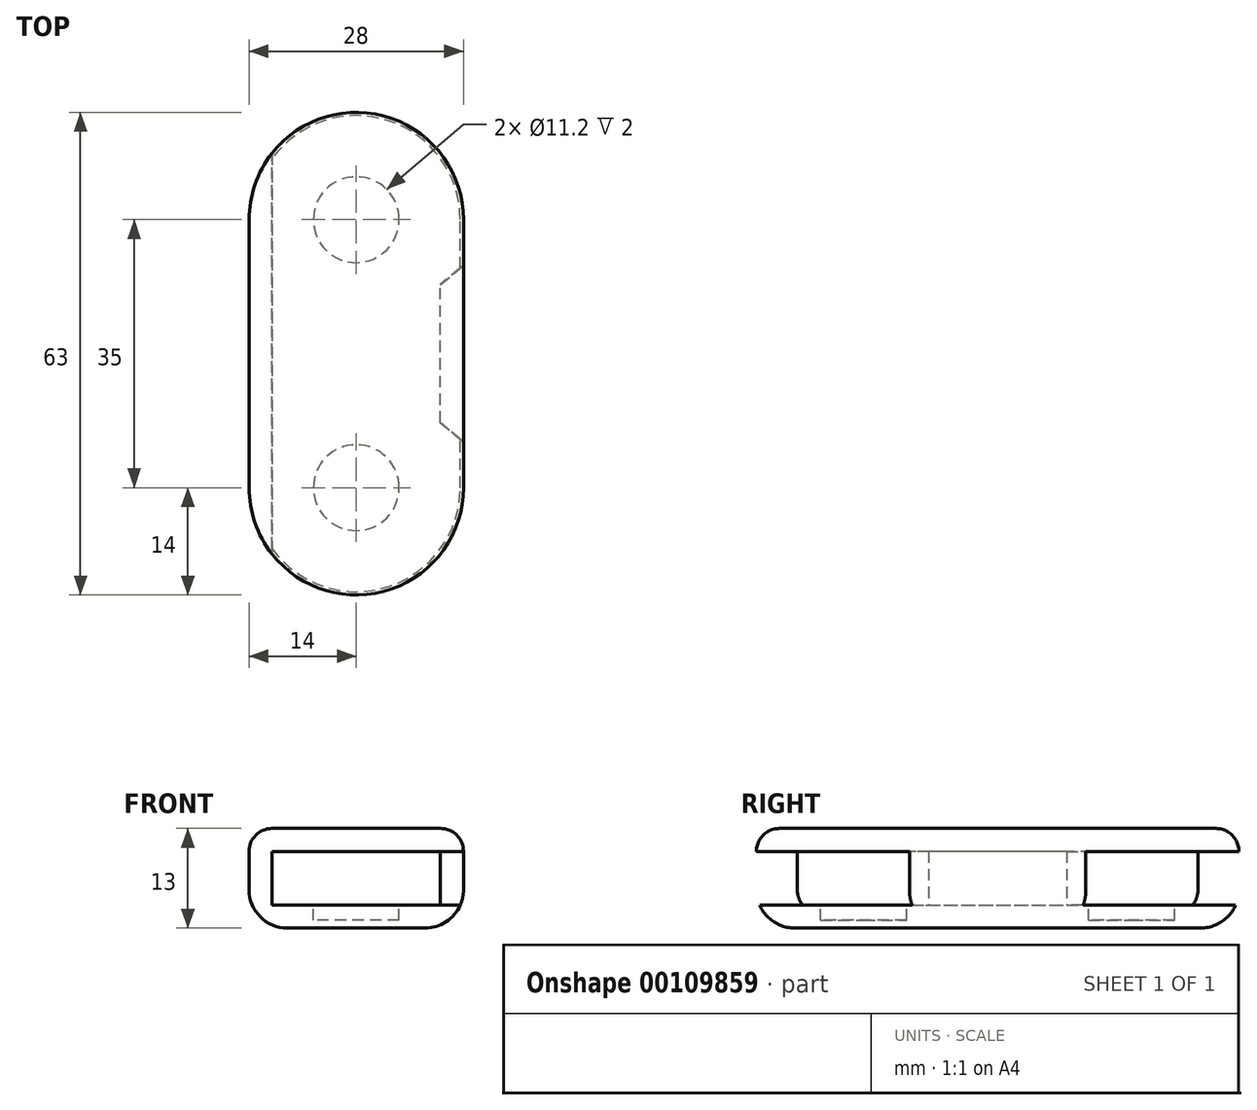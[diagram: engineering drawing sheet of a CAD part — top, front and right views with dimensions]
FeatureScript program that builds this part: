
annotation { "Feature Type Name" : "Feature", "Feature Type Description" : "" }
export const myFeature = defineFeature(function(context is Context, id is Id, definition is map)
    precondition{}
    {
        {
            var Q0;
            Q0=qCreatedBy(makeId("Top.planeOp"),FACE);
            var sketch = newSketch(context, id + "F0", { "sketchPlane" : qUnion([Q0])});
            skCircle(sketch, "E0", {"center": v(0, 17.5) * mm, "radius": 5.6 * mm, "construction": true});
            skCircle(sketch, "E1", {"center": v(0, -17.5) * mm, "radius": 5.6 * mm, "construction": true});
            skLineSegment(sketch, "E2", {"start": v(0, 17.5) * mm, "end": v(0, -17.5) * mm, "construction": true});
            skArc(sketch, "E3", {"start": v(11, 17.5) * mm, "mid": v(0, 28.5) * mm, "end": v(-11, 17.5) * mm, "construction": true});
            skArc(sketch, "E4", {"start": v(-11, -17.5) * mm, "mid": v(0, -28.5) * mm, "end": v(11, -17.5) * mm, "construction": true});
            skLineSegment(sketch, "E5", {"start": v(-11, 17.5) * mm, "end": v(-11, -17.5) * mm, "construction": true});
            skLineSegment(sketch, "E6", {"start": v(11, 17.5) * mm, "end": v(11, -17.5) * mm, "construction": true});
            skArc(sketch, "E7.0", {"start": v(14, 17.5) * mm, "mid": v(0, 31.5) * mm, "end": v(-14, 17.5) * mm});
            skLineSegment(sketch, "E7.1", {"start": v(14, 17.5) * mm, "end": v(14, -17.5) * mm});
            skArc(sketch, "E7.2", {"start": v(-14, -17.5) * mm, "mid": v(0, -31.5) * mm, "end": v(14, -17.5) * mm});
            skLineSegment(sketch, "E7.3", {"start": v(-14, 17.5) * mm, "end": v(-14, -17.5) * mm});
            skLineSegment(sketch, "E8", {"start": v(-9, 25.87) * mm, "end": v(7.6, 32.12) * mm, "construction": true});
            skLineSegment(sketch, "E9", {"start": v(-9, -25.87) * mm, "end": v(7.6, -32.12) * mm, "construction": true});
            skArc(sketch, "E10", {"start": v(-15.3, 18.34) * mm, "mid": v(-17, 0) * mm, "end": v(-15.3, -18.34) * mm, "construction": true});
            skArc(sketch, "E11", {"start": v(15.66, 25.73) * mm, "mid": v(14, 0) * mm, "end": v(15.66, -25.73) * mm, "construction": true});
            skArc(sketch, "E12", {"start": v(7.6, 32.12) * mm, "mid": v(13.44, 31.2) * mm, "end": v(15.66, 25.73) * mm, "construction": true});
            skArc(sketch, "E13", {"start": v(7.6, -32.12) * mm, "mid": v(13.44, -31.2) * mm, "end": v(15.66, -25.73) * mm, "construction": true});
            skLineSegment(sketch, "E14", {"start": v(0, 0) * mm, "end": v(83, 0) * mm, "construction": true});
            skLineSegment(sketch, "E15", {"start": v(9.71, 26.5) * mm, "end": v(9.71, -26.5) * mm, "construction": true});
            skPoint(sketch, "E16.visualSharp", {"position": v(-14.1, 23.95) * mm});
            skArc(sketch, "E16.filletArc", {"start": v(-9, 25.87) * mm, "mid": v(-13.14, 22.93) * mm, "end": v(-15.3, 18.34) * mm, "construction": true});
            skPoint(sketch, "E17.visualSharp", {"position": v(-14.1, -23.95) * mm});
            skArc(sketch, "E17.filletArc", {"start": v(-15.3, -18.34) * mm, "mid": v(-13.14, -22.93) * mm, "end": v(-9, -25.87) * mm, "construction": true});
            skSolve(sketch);
        }
        {
            var Q0;
            Q0=makeQuery(id+"F0.imprint","IMPRINT",FACE,{"disambiguationData":[TD([[makeQuery(id+"F0.imprint","IMPRINT",EDGE,{"derivedFrom":sQuery(id+"F0.wireOp",EDGE,"E7.0")}),1.0]])]});
            extrude(context, id + "F1", {"entities" : qUnion([Q0]), "depth" : 3 * mm});
        }
        {
            var Q0;
            Q0=makeQuery(id+"F1.opExtrude","CAP_FACE",FACE,{"disambiguationData":[OSD([sQuery(id+"F0.wireOp",EDGE,"E7.0"),sQuery(id+"F0.wireOp",EDGE,"E7.1"),sQuery(id+"F0.wireOp",EDGE,"E7.2"),sQuery(id+"F0.wireOp",EDGE,"E7.3")])],"isStart":false});
            var sketch = newSketch(context, id + "F2", { "sketchPlane" : qUnion([Q0])});
            skCircle(sketch, "E18", {"center": v(0, 17.5) * mm, "radius": 5.6 * mm});
            skCircle(sketch, "E19", {"center": v(0, -17.5) * mm, "radius": 5.6 * mm});
            skLineSegment(sketch, "E20", {"start": v(0, 17.5) * mm, "end": v(0, -17.5) * mm, "construction": true});
            skArc(sketch, "E21", {"start": v(11, 17.5) * mm, "mid": v(0, 28.5) * mm, "end": v(-11, 17.5) * mm, "construction": true});
            skArc(sketch, "E22", {"start": v(-11, -17.5) * mm, "mid": v(0, -28.5) * mm, "end": v(11, -17.5) * mm, "construction": true});
            skLineSegment(sketch, "E23", {"start": v(-11, 17.5) * mm, "end": v(-11, -17.5) * mm, "construction": true});
            skLineSegment(sketch, "E24", {"start": v(11, 17.5) * mm, "end": v(11, -17.5) * mm, "construction": true});
            skArc(sketch, "E25.0", {"start": v(14, 17.5) * mm, "mid": v(0, 31.5) * mm, "end": v(-14, 17.5) * mm});
            skLineSegment(sketch, "E25.1", {"start": v(14, 17.5) * mm, "end": v(14, -17.5) * mm});
            skArc(sketch, "E25.2", {"start": v(-14, -17.5) * mm, "mid": v(0, -31.5) * mm, "end": v(14, -17.5) * mm});
            skLineSegment(sketch, "E25.3", {"start": v(-14, 17.5) * mm, "end": v(-14, -17.5) * mm});
            skLineSegment(sketch, "E26", {"start": v(-7.8, 25.97) * mm, "end": v(13.49, 36.11) * mm, "construction": true});
            skLineSegment(sketch, "E27", {"start": v(-7.8, -25.97) * mm, "end": v(13.49, -36.11) * mm, "construction": true});
            skArc(sketch, "E28", {"start": v(-10.24, 23.4) * mm, "mid": v(-15, 0) * mm, "end": v(-10.24, -23.4) * mm, "construction": true});
            skArc(sketch, "E29", {"start": v(19, 31.25) * mm, "mid": v(14, 0) * mm, "end": v(19, -31.25) * mm, "construction": true});
            skArc(sketch, "E30", {"start": v(13.49, 36.11) * mm, "mid": v(17.85, 35.5) * mm, "end": v(19, 31.25) * mm, "construction": true});
            skArc(sketch, "E31", {"start": v(13.49, -36.11) * mm, "mid": v(17.85, -35.5) * mm, "end": v(19, -31.25) * mm, "construction": true});
            skLineSegment(sketch, "E32", {"start": v(0, 0) * mm, "end": v(45, 0) * mm, "construction": true});
            skLineSegment(sketch, "E33", {"start": v(15.2, 32.5) * mm, "end": v(15.2, -32.5) * mm, "construction": true});
            skPoint(sketch, "E34.visualSharp", {"position": v(-9.46, 25.18) * mm});
            skArc(sketch, "E34.filletArc", {"start": v(-7.8, 25.97) * mm, "mid": v(-9.25, 24.92) * mm, "end": v(-10.24, 23.4) * mm, "construction": true});
            skPoint(sketch, "E35.visualSharp", {"position": v(-9.46, -25.18) * mm});
            skArc(sketch, "E35.filletArc", {"start": v(-10.24, -23.4) * mm, "mid": v(-9.25, -24.92) * mm, "end": v(-7.8, -25.97) * mm, "construction": true});
            skSolve(sketch);
        }
        {
            var Q0;
            Q0=makeQuery(id+"F2.imprint","IMPRINT",FACE,{"disambiguationData":[TD([[makeQuery(id+"F2.imprint","IMPRINT",EDGE,{"derivedFrom":sQuery(id+"F2.wireOp",EDGE,"E18")}),1.0]])]});
            var Q1;
            Q1=makeQuery(id+"F2.imprint","IMPRINT",FACE,{"disambiguationData":[TD([[makeQuery(id+"F2.imprint","IMPRINT",EDGE,{"derivedFrom":sQuery(id+"F2.wireOp",EDGE,"E19")}),1.0]])]});
            extrude(context, id + "F3", {"entities" : qUnion([Q0, Q1]), "operationType" : NewBodyOperationType.REMOVE, "oppositeDirection" : true, "depth" : 2 * mm});
        }
        {
            var Q0;
            Q0=qCreatedBy(makeId("Top.planeOp"),FACE);
            var sketch = newSketch(context, id + "F4", { "sketchPlane" : qUnion([Q0])});
            skCircle(sketch, "E36", {"center": v(0, 17.5) * mm, "radius": 5.6 * mm, "construction": true});
            skCircle(sketch, "E37", {"center": v(0, -17.5) * mm, "radius": 5.6 * mm, "construction": true});
            skLineSegment(sketch, "E38", {"start": v(0, 17.5) * mm, "end": v(0, -17.5) * mm, "construction": true});
            skArc(sketch, "E39", {"start": v(11, 17.5) * mm, "mid": v(0, 28.5) * mm, "end": v(-11, 17.5) * mm, "construction": true});
            skArc(sketch, "E40", {"start": v(-11, -17.5) * mm, "mid": v(0, -28.5) * mm, "end": v(11, -17.5) * mm, "construction": true});
            skLineSegment(sketch, "E41", {"start": v(-11, 26.16) * mm, "end": v(-11, -26.16) * mm});
            skLineSegment(sketch, "E42", {"start": v(11, 9) * mm, "end": v(11, -9) * mm});
            skArc(sketch, "E43.0", {"start": v(14, 17.5) * mm, "mid": v(0, 31.5) * mm, "end": v(-14, 17.5) * mm});
            skLineSegment(sketch, "E43.1", {"start": v(14, 17.5) * mm, "end": v(14, -17.5) * mm});
            skArc(sketch, "E43.2", {"start": v(-14, -17.5) * mm, "mid": v(0, -31.5) * mm, "end": v(14, -17.5) * mm});
            skLineSegment(sketch, "E43.3", {"start": v(-14, 17.5) * mm, "end": v(-14, -17.5) * mm});
            skLineSegment(sketch, "E44", {"start": v(0, 0) * mm, "end": v(43, 0) * mm, "construction": true});
            skLineSegment(sketch, "E45", {"start": v(15.2, 32.5) * mm, "end": v(15.2, -32.5) * mm, "construction": true});
            skPoint(sketch, "E46.orphan", {"position": v(7.6, 32.12) * mm});
            skPoint(sketch, "E47.orphan", {"position": v(7.6, -32.12) * mm});
            skLineSegment(sketch, "E48", {"start": v(11, 9) * mm, "end": v(14, 11.52) * mm});
            skLineSegment(sketch, "E49.MirrorCS", {"start": v(11, -9) * mm, "end": v(14, -11.52) * mm});
            skPoint(sketch, "E50.orphan", {"position": v(15.66, -25.73) * mm});
            skPoint(sketch, "E51.orphan", {"position": v(15.66, 25.73) * mm});
            skSolve(sketch);
        }
        {
            var Q0;
            {var subQ0=sQuery(id+"F4.wireOp",EDGE,"E41");Q0=makeQuery(id+"F4.imprint","IMPRINT",FACE,{"disambiguationData":[TD([[makeQuery(id+"F4.imprint","IMPRINT",EDGE,{"derivedFrom":subQ0}),-1.0]])]});}
            var Q1;
            Q1=makeQuery(id+"F4.imprint","IMPRINT",FACE,{"disambiguationData":[TD([[makeQuery(id+"F4.imprint","IMPRINT",EDGE,{"derivedFrom":sQuery(id+"F4.wireOp",EDGE,"E42")}),1.0]])]});
            extrude(context, id + "F5", {"entities" : qUnion([Q0, Q1]), "operationType" : NewBodyOperationType.ADD, "depth" : 10 * mm});
        }
        {
            var Q0;
            Q0=makeQuery(id+"F5.opExtrude","CAP_FACE",FACE,{"disambiguationData":[OSD([sQuery(id+"F4.wireOp",EDGE,"E41"),sQuery(id+"F4.wireOp",EDGE,"fcb67851-2fee-4d54-8a3d-cb105869aaa7"),sQuery(id+"F4.wireOp",EDGE,"5d6f1e88-396b-45d1-9be9-a47ba8d2432e"),sQuery(id+"F4.wireOp",EDGE,"66534eae-351e-46f8-825e-5522550ca6c2")])],"isStart":false});
            var sketch = newSketch(context, id + "F6", { "sketchPlane" : qUnion([Q0])});
            skLineSegment(sketch, "E52.0.0", {"start": v(-12.56, 23.11) * mm, "end": v(10.66, 36) * mm, "construction": true});
            skArc(sketch, "E52.0.1", {"start": v(10.66, 36) * mm, "mid": v(14.9, 35.77) * mm, "end": v(16.55, 31.86) * mm, "construction": true});
            skArc(sketch, "E52.0.2", {"start": v(16.55, 31.86) * mm, "mid": v(14, 0) * mm, "end": v(16.55, -31.86) * mm, "construction": true});
            skArc(sketch, "E52.0.3", {"start": v(16.55, -31.86) * mm, "mid": v(14.9, -35.77) * mm, "end": v(10.66, -36) * mm, "construction": true});
            skLineSegment(sketch, "E52.0.4", {"start": v(10.66, -36) * mm, "end": v(-12.56, -23.11) * mm, "construction": true});
            skArc(sketch, "E52.0.5", {"start": v(-12.56, -23.11) * mm, "mid": v(-14.17, -21.7) * mm, "end": v(-15.04, -19.73) * mm, "construction": true});
            skArc(sketch, "E52.0.7", {"start": v(-15.04, 19.73) * mm, "mid": v(-14.17, 21.7) * mm, "end": v(-12.56, 23.11) * mm, "construction": true});
            skArc(sketch, "E53.0", {"start": v(-15.04, 19.73) * mm, "mid": v(-18.3, 0) * mm, "end": v(-15.04, -19.73) * mm, "construction": true});
            skLineSegment(sketch, "E54.0.0", {"start": v(14, 17.5) * mm, "end": v(14, -17.5) * mm});
            skArc(sketch, "E54.0.1", {"start": v(14, -17.5) * mm, "mid": v(0, -31.5) * mm, "end": v(-14, -17.5) * mm});
            skLineSegment(sketch, "E54.0.2", {"start": v(-14, -17.5) * mm, "end": v(-14, 17.5) * mm});
            skArc(sketch, "E54.0.3", {"start": v(-14, 17.5) * mm, "mid": v(0, 31.5) * mm, "end": v(14, 17.5) * mm});
            skSolve(sketch);
        }
        {
            var Q0;
            {var subQ0=sQuery(id+"F6.wireOp",EDGE,"E54.0.0");Q0=makeQuery(id+"F6.imprint","IMPRINT",FACE,{"disambiguationData":[TD([[makeQuery(id+"F6.imprint","IMPRINT",EDGE,{"derivedFrom":subQ0}),-1.0]])]});}
            var Q1;
            {var subQ2=sQuery(id+"F6.wireOp",EDGE,"E54.0.2");Q1=makeQuery(id+"F6.imprint","IMPRINT",FACE,{"disambiguationData":[TD([[makeQuery(id+"F6.imprint","IMPRINT",EDGE,{"derivedFrom":subQ2}),1.0]])]});}
            extrude(context, id + "F7", {"entities" : qUnion([Q0, Q1]), "operationType" : NewBodyOperationType.ADD, "depth" : 3 * mm});
        }
        {
            var Q0;
            Q0=makeQuery(id+"F7.opExtrude","CAP_FACE",FACE,{"disambiguationData":[OSD([sQuery(id+"F6.wireOp",EDGE,"E54.0.0"),sQuery(id+"F6.wireOp",EDGE,"E54.0.1"),sQuery(id+"F6.wireOp",EDGE,"E54.0.2"),sQuery(id+"F6.wireOp",EDGE,"E54.0.3")])],"isStart":false});
            fillet(context, id + "F8", {"entities" : qUnion([Q0]), "radius" : 3 * mm, "tangentPropagation" : true, "allowEdgeOverflow" : false});
        }
        {
            var Q0;
            Q0=makeQuery(id+"F1.opExtrude","CAP_FACE",FACE,{"disambiguationData":[OSD([sQuery(id+"F0.wireOp",EDGE,"E7.0"),sQuery(id+"F0.wireOp",EDGE,"E7.1"),sQuery(id+"F0.wireOp",EDGE,"E7.2"),sQuery(id+"F0.wireOp",EDGE,"E7.3")])],"isStart":true});
            fillet(context, id + "F9", {"entities" : qUnion([Q0]), "radius" : 5 * mm, "tangentPropagation" : true, "allowEdgeOverflow" : false});
        }
    });
